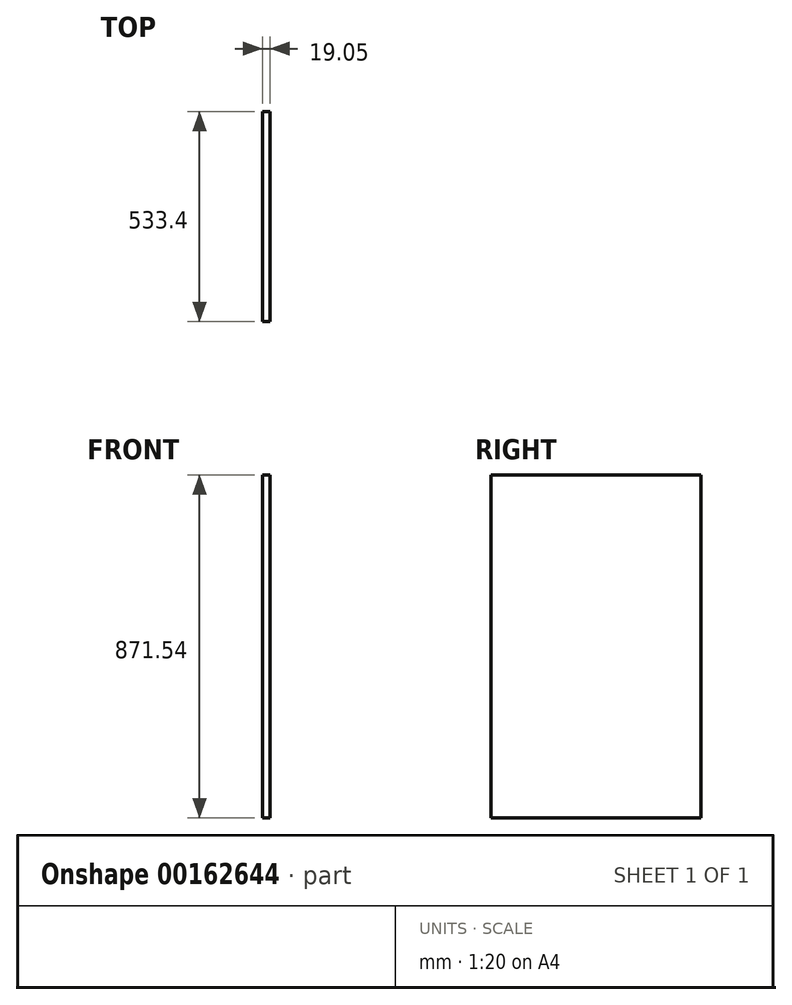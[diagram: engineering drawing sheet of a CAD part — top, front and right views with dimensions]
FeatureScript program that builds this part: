
annotation { "Feature Type Name" : "Feature", "Feature Type Description" : "" }
export const myFeature = defineFeature(function(context is Context, id is Id, definition is map)
    precondition{}
    {
        {
            var Q0;
            Q0=qCreatedBy(makeId("Right.planeOp"),FACE);
            var sketch = newSketch(context, id + "F0", { "sketchPlane" : qUnion([Q0])});
            skLineSegment(sketch, "E0.bottom", {"start": v(-368.83, 418.54) * mm, "end": v(164.57, 418.54) * mm});
            skLineSegment(sketch, "E0.top", {"start": v(-368.83, -453) * mm, "end": v(164.57, -453) * mm});
            skLineSegment(sketch, "E0.left", {"start": v(-368.83, 418.54) * mm, "end": v(-368.83, -453) * mm});
            skLineSegment(sketch, "E0.right", {"start": v(164.57, 418.54) * mm, "end": v(164.57, -453) * mm});
            skSolve(sketch);
        }
        {
            var Q0;
            Q0 = qSketchRegion(id + "F0", true);
            extrude(context, id + "F1", {"entities" : qUnion([Q0]), "depth" : 19.05 * mm});
        }
    });
